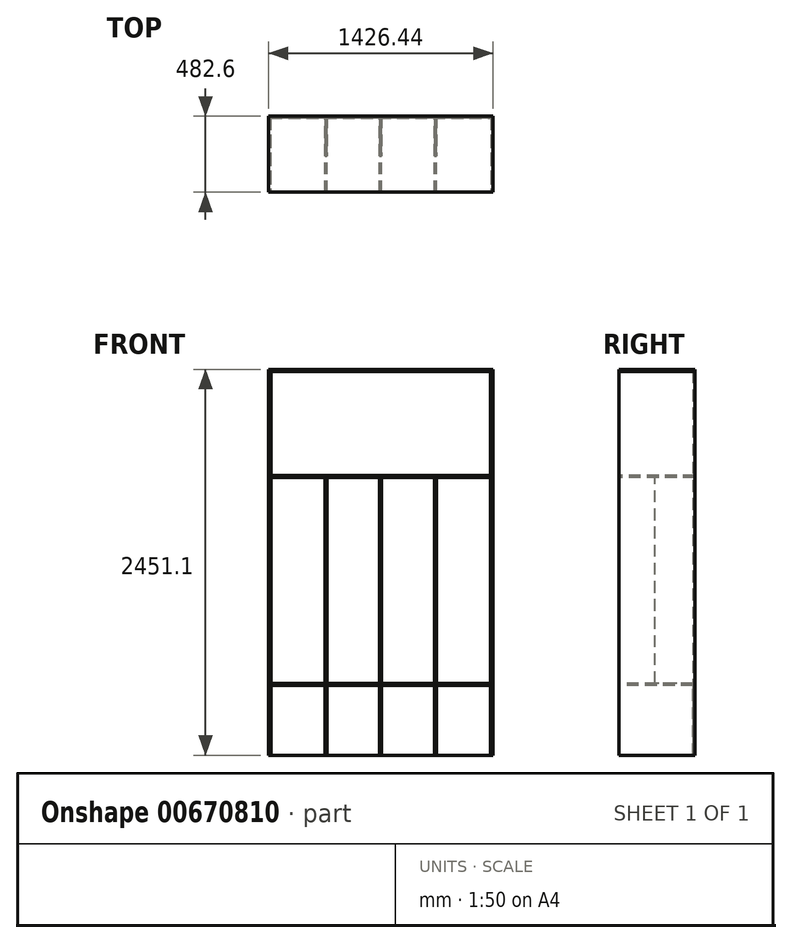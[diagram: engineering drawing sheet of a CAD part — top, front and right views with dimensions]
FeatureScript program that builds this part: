
annotation { "Feature Type Name" : "Feature", "Feature Type Description" : "" }
export const myFeature = defineFeature(function(context is Context, id is Id, definition is map)
    precondition{}
    {
        {
            var Q0;
            Q0=qCreatedBy(makeId("Front.planeOp"),FACE);
            var sketch = newSketch(context, id + "F0", { "sketchPlane" : qUnion([Q0])});
            skLineSegment(sketch, "E0.bottom", {"start": v(-700.52, 1580.9) * mm, "end": v(696.48, 1580.9) * mm});
            skLineSegment(sketch, "E0.top", {"start": v(-700.52, -857.5) * mm, "end": v(696.48, -857.5) * mm});
            skLineSegment(sketch, "E0.left", {"start": v(-700.52, 1580.9) * mm, "end": v(-700.52, -857.5) * mm});
            skLineSegment(sketch, "E0.right", {"start": v(696.48, 1580.9) * mm, "end": v(696.48, -857.5) * mm});
            skSolve(sketch);
        }
        {
            var Q0;
            Q0 = qSketchRegion(id + "F0", true);
            extrude(context, id + "F1", {"entities" : qUnion([Q0]), "depth" : 12.7 * mm, "offsetDistance" : 25.4 * mm});
        }
        {
            var Q0;
            Q0=makeQuery(id+"F1.opExtrude","SWEPT_FACE",FACE,{"disambiguationData":[OSD([sQuery(id+"F0.wireOp",EDGE,"E0.left")])]});
            var sketch = newSketch(context, id + "F2", { "sketchPlane" : qUnion([Q0])});
            skLineSegment(sketch, "E1.bottom", {"start": v(0, 1580.9) * mm, "end": v(482.6, 1580.9) * mm});
            skLineSegment(sketch, "E1.top", {"start": v(0, -857.5) * mm, "end": v(482.6, -857.5) * mm});
            skLineSegment(sketch, "E1.left", {"start": v(0, 1580.9) * mm, "end": v(0, -857.5) * mm});
            skLineSegment(sketch, "E1.right", {"start": v(482.6, 1580.9) * mm, "end": v(482.6, -857.5) * mm});
            skSolve(sketch);
        }
        {
            var Q0;
            Q0 = qSketchRegion(id + "F2", true);
            extrude(context, id + "F3", {"entities" : qUnion([Q0]), "operationType" : NewBodyOperationType.ADD, "depth" : 12.7 * mm, "offsetDistance" : 25.4 * mm});
        }
        {
            var Q0;
            Q0=makeQuery(id+"F1.opExtrude","SWEPT_BODY",BODY,{"disambiguationData":[OSD([sQuery(id+"F0.wireOp",EDGE,"E0.bottom"),sQuery(id+"F0.wireOp",EDGE,"E0.top"),sQuery(id+"F0.wireOp",EDGE,"E0.left"),sQuery(id+"F0.wireOp",EDGE,"E0.right")])]});
            var Q1;
            Q1=qCreatedBy(makeId("Right.planeOp"),FACE);
            mirror(context, id + "F4", {"entities" : qUnion([Q0]), "mirrorPlane" : qUnion([Q1])});
        }
        {
            var Q0;
            Q0=makeQuery(id+"F3.boolean.opBoolean","MERGE",FACE,{"derivedFrom":[makeQuery(id+"F1.opExtrude","SWEPT_FACE",FACE,{"disambiguationData":[OSD([sQuery(id+"F0.wireOp",EDGE,"E0.bottom")])]}),makeQuery(id+"F3.opExtrude","SWEPT_FACE",FACE,{"disambiguationData":[OSD([sQuery(id+"F2.wireOp",EDGE,"E1.bottom")])]})]});
            var sketch = newSketch(context, id + "F5", { "sketchPlane" : qUnion([Q0])});
            skLineSegment(sketch, "E2.bottom", {"start": v(-713.22, 0) * mm, "end": v(713.22, 0) * mm});
            skLineSegment(sketch, "E2.top", {"start": v(-713.22, -482.6) * mm, "end": v(713.22, -482.6) * mm});
            skLineSegment(sketch, "E2.left", {"start": v(-713.22, 0) * mm, "end": v(-713.22, -482.6) * mm});
            skLineSegment(sketch, "E2.right", {"start": v(713.22, 0) * mm, "end": v(713.22, -482.6) * mm});
            skPoint(sketch, "E3.left.start.orphan", {"position": v(619.43, -567.36) * mm});
            skPoint(sketch, "E3.right.start.orphan", {"position": v(696.86, -567.36) * mm});
            skPoint(sketch, "E4.right.end.orphan", {"position": v(658.15, -567.36) * mm});
            skSolve(sketch);
        }
        {
            var Q0;
            Q0 = qSketchRegion(id + "F5", true);
            extrude(context, id + "F6", {"entities" : qUnion([Q0]), "depth" : 12.7 * mm, "offsetDistance" : 25.4 * mm});
        }
        {
            var Q0;
            Q0=makeQuery(id+"F4.opPattern","COPY",FACE,{"derivedFrom":makeQuery(id+"F3.boolean.opBoolean","MERGE",FACE,{"derivedFrom":[makeQuery(id+"F1.opExtrude","SWEPT_FACE",FACE,{"disambiguationData":[OSD([sQuery(id+"F0.wireOp",EDGE,"E0.top")])]}),makeQuery(id+"F3.opExtrude","SWEPT_FACE",FACE,{"disambiguationData":[OSD([sQuery(id+"F2.wireOp",EDGE,"E1.top")])]})]}),"instanceName":"1"});
            cPlane(context, id + "F7", {"entities" : qUnion([Q0]), "cplaneType" : CPlaneType.OFFSET, "offset" : 457.2 * mm, "oppositeDirection" : true, "width" : 152.4 * mm, "height" : 152.4 * mm});
        }
        {
            var Q0;
            Q0=qCreatedBy(id+"F7.planeOp",FACE);
            var sketch = newSketch(context, id + "F8", { "sketchPlane" : qUnion([Q0])});
            skLineSegment(sketch, "E5.bottom", {"start": v(-700.52, 12.7) * mm, "end": v(700.52, 12.7) * mm});
            skLineSegment(sketch, "E5.top", {"start": v(-700.52, 482.6) * mm, "end": v(700.52, 482.6) * mm});
            skLineSegment(sketch, "E5.left", {"start": v(-700.52, 12.7) * mm, "end": v(-700.52, 482.6) * mm});
            skLineSegment(sketch, "E5.right", {"start": v(700.52, 12.7) * mm, "end": v(700.52, 482.6) * mm});
            skSolve(sketch);
        }
        {
            var Q0;
            Q0 = qSketchRegion(id + "F8", true);
            extrude(context, id + "F9", {"entities" : qUnion([Q0]), "depth" : 12.7 * mm, "offsetDistance" : 25.4 * mm});
        }
        {
            var Q0;
            Q0=makeQuery(id+"F3.boolean.opBoolean","MERGE",FACE,{"derivedFrom":[makeQuery(id+"F1.opExtrude","SWEPT_FACE",FACE,{"disambiguationData":[OSD([sQuery(id+"F0.wireOp",EDGE,"E0.top")])]}),makeQuery(id+"F3.opExtrude","SWEPT_FACE",FACE,{"disambiguationData":[OSD([sQuery(id+"F2.wireOp",EDGE,"E1.top")])]})]});
            cPlane(context, id + "F10", {"entities" : qUnion([Q0]), "cplaneType" : CPlaneType.OFFSET, "offset" : 1778 * mm, "oppositeDirection" : true, "width" : 152.4 * mm, "height" : 152.4 * mm});
        }
        {
            var Q0;
            Q0=qCreatedBy(id+"F10.planeOp",FACE);
            var sketch = newSketch(context, id + "F11", { "sketchPlane" : qUnion([Q0])});
            skLineSegment(sketch, "E6.bottom", {"start": v(-700.52, 0) * mm, "end": v(700.52, 0) * mm});
            skLineSegment(sketch, "E6.top", {"start": v(-700.52, 482.6) * mm, "end": v(700.52, 482.6) * mm});
            skLineSegment(sketch, "E6.left", {"start": v(-700.52, 0) * mm, "end": v(-700.52, 482.6) * mm});
            skLineSegment(sketch, "E6.right", {"start": v(700.52, 0) * mm, "end": v(700.52, 482.6) * mm});
            skSolve(sketch);
        }
        {
            var Q0;
            Q0=makeQuery(id+"F11.imprint","IMPRINT",FACE,{"disambiguationData":[TD([[makeQuery(id+"F11.imprint","IMPRINT",EDGE,{"derivedFrom":sQuery(id+"F11.wireOp",EDGE,"E6.bottom")}),1.0]])]});
            extrude(context, id + "F12", {"entities" : qUnion([Q0]), "depth" : 12.7 * mm, "offsetDistance" : 25.4 * mm});
        }
        {
            var Q0;
            Q0=makeQuery(id+"F12.opExtrude","CAP_FACE",FACE,{"disambiguationData":[OSD([sQuery(id+"F11.wireOp",EDGE,"E6.bottom"),sQuery(id+"F11.wireOp",EDGE,"E6.top"),sQuery(id+"F11.wireOp",EDGE,"E6.left"),sQuery(id+"F11.wireOp",EDGE,"E6.right")])],"isStart":false});
            var sketch = newSketch(context, id + "F13", { "sketchPlane" : qUnion([Q0])});
            skLineSegment(sketch, "E7.bottom", {"start": v(-353.44, 0) * mm, "end": v(-340.74, 0) * mm});
            skLineSegment(sketch, "E7.top", {"start": v(-353.44, 254) * mm, "end": v(-340.74, 254) * mm});
            skLineSegment(sketch, "E7.left", {"start": v(-340.74, 0) * mm, "end": v(-340.74, 254) * mm});
            skLineSegment(sketch, "E7.right", {"start": v(-353.44, 0) * mm, "end": v(-353.44, 254) * mm});
            skLineSegment(sketch, "E8.bottom", {"start": v(-6.35, 0) * mm, "end": v(6.35, 0) * mm});
            skLineSegment(sketch, "E8.top", {"start": v(-6.35, 254) * mm, "end": v(6.35, 254) * mm});
            skLineSegment(sketch, "E8.left", {"start": v(6.35, 0) * mm, "end": v(6.35, 254) * mm});
            skLineSegment(sketch, "E8.right", {"start": v(-6.35, 0) * mm, "end": v(-6.35, 254) * mm});
            skLineSegment(sketch, "E9.bottom", {"start": v(340.74, 0) * mm, "end": v(353.44, 0) * mm});
            skLineSegment(sketch, "E9.top", {"start": v(340.74, 254) * mm, "end": v(353.44, 254) * mm});
            skLineSegment(sketch, "E9.left", {"start": v(353.44, 0) * mm, "end": v(353.44, 254) * mm});
            skLineSegment(sketch, "E9.right", {"start": v(340.74, 0) * mm, "end": v(340.74, 254) * mm});
            skLineSegment(sketch, "E10", {"start": v(-340.74, 0) * mm, "end": v(-700.52, 0) * mm, "construction": true});
            skLineSegment(sketch, "E11", {"start": v(-353.44, 0) * mm, "end": v(6.35, 0) * mm, "construction": true});
            skLineSegment(sketch, "E12", {"start": v(-6.35, 0) * mm, "end": v(353.44, 0) * mm, "construction": true});
            skLineSegment(sketch, "E13", {"start": v(340.74, 0) * mm, "end": v(700.52, 0) * mm, "construction": true});
            skSolve(sketch);
        }
        {
            var Q0;
            Q0 = qSketchRegion(id + "F13", true);
            var Q1;
            Q1=makeQuery(id+"F9.opExtrude","CAP_FACE",FACE,{"disambiguationData":[OSD([sQuery(id+"F8.wireOp",EDGE,"E5.bottom"),sQuery(id+"F8.wireOp",EDGE,"E5.top"),sQuery(id+"F8.wireOp",EDGE,"E5.left"),sQuery(id+"F8.wireOp",EDGE,"E5.right")])],"isStart":true});
            extrude(context, id + "F14", {"entities" : qUnion([Q0]), "endBound" : BoundingType.UP_TO_SURFACE, "depth" : 25.4 * mm, "endBoundEntityFace" : qUnion([Q1]), "offsetDistance" : 25.4 * mm});
        }
        {
            var Q0;
            Q0=makeQuery(id+"F9.opExtrude","CAP_FACE",FACE,{"disambiguationData":[OSD([sQuery(id+"F8.wireOp",EDGE,"E5.bottom"),sQuery(id+"F8.wireOp",EDGE,"E5.top"),sQuery(id+"F8.wireOp",EDGE,"E5.left"),sQuery(id+"F8.wireOp",EDGE,"E5.right")])],"isStart":false});
            var sketch = newSketch(context, id + "F15", { "sketchPlane" : qUnion([Q0])});
            skLineSegment(sketch, "E14.bottom", {"start": v(-353.44, 12.7) * mm, "end": v(-340.74, 12.7) * mm});
            skLineSegment(sketch, "E14.top", {"start": v(-353.44, 482.6) * mm, "end": v(-340.74, 482.6) * mm});
            skLineSegment(sketch, "E14.left", {"start": v(-353.44, 12.7) * mm, "end": v(-353.44, 482.6) * mm});
            skLineSegment(sketch, "E14.right", {"start": v(-340.74, 12.7) * mm, "end": v(-340.74, 482.6) * mm});
            skLineSegment(sketch, "E15.bottom", {"start": v(-6.35, 12.7) * mm, "end": v(6.35, 12.7) * mm});
            skLineSegment(sketch, "E15.top", {"start": v(-6.35, 482.6) * mm, "end": v(6.35, 482.6) * mm});
            skLineSegment(sketch, "E15.left", {"start": v(-6.35, 12.7) * mm, "end": v(-6.35, 482.6) * mm});
            skLineSegment(sketch, "E15.right", {"start": v(6.35, 12.7) * mm, "end": v(6.35, 482.6) * mm});
            skLineSegment(sketch, "E16.bottom", {"start": v(340.74, 12.7) * mm, "end": v(353.44, 12.7) * mm});
            skLineSegment(sketch, "E16.top", {"start": v(340.74, 482.6) * mm, "end": v(353.44, 482.6) * mm});
            skLineSegment(sketch, "E16.left", {"start": v(340.74, 12.7) * mm, "end": v(340.74, 482.6) * mm});
            skLineSegment(sketch, "E16.right", {"start": v(353.44, 12.7) * mm, "end": v(353.44, 482.6) * mm});
            skSolve(sketch);
        }
        {
            var Q0;
            Q0 = qSketchRegion(id + "F15", true);
            var Q1;
            Q1=makeQuery(id+"F3.boolean.opBoolean","MERGE",FACE,{"derivedFrom":[makeQuery(id+"F1.opExtrude","SWEPT_FACE",FACE,{"disambiguationData":[OSD([sQuery(id+"F0.wireOp",EDGE,"E0.top")])]}),makeQuery(id+"F3.opExtrude","SWEPT_FACE",FACE,{"disambiguationData":[OSD([sQuery(id+"F2.wireOp",EDGE,"E1.top")])]})]});
            extrude(context, id + "F16", {"entities" : qUnion([Q0]), "endBound" : BoundingType.UP_TO_SURFACE, "depth" : 25.4 * mm, "endBoundEntityFace" : qUnion([Q1]), "offsetDistance" : 25.4 * mm});
        }
    });
